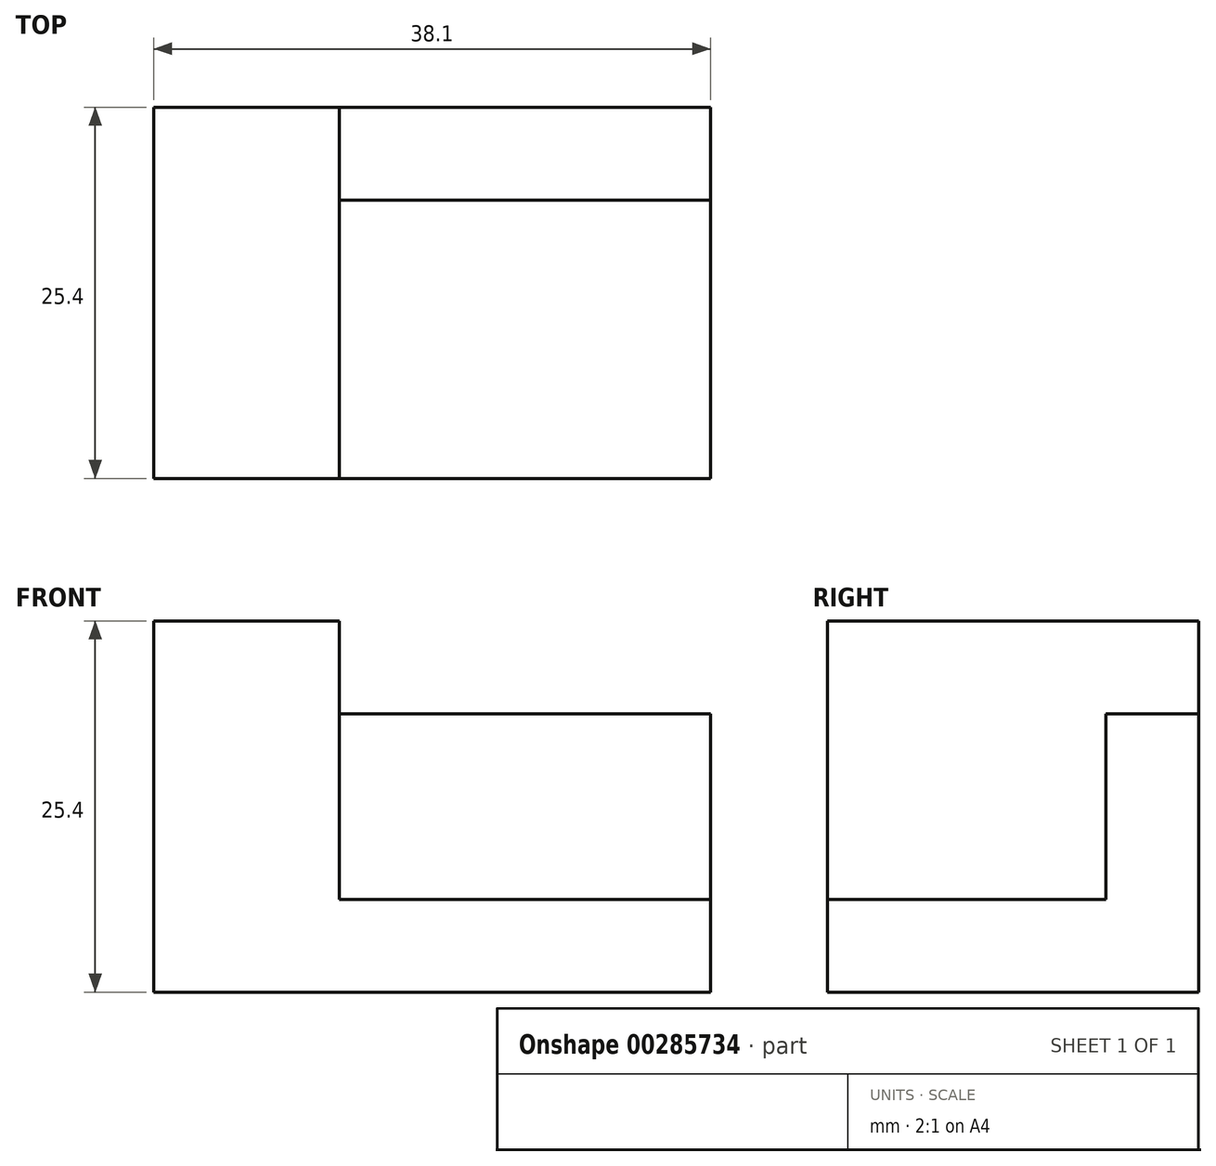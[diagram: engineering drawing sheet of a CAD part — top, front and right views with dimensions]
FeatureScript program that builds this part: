
annotation { "Feature Type Name" : "Feature", "Feature Type Description" : "" }
export const myFeature = defineFeature(function(context is Context, id is Id, definition is map)
    precondition{}
    {
        {
            var Q0;
            Q0=qCreatedBy(makeId("Front.planeOp"),FACE);
            var sketch = newSketch(context, id + "F0", { "sketchPlane" : qUnion([Q0])});
            skLineSegment(sketch, "E0", {"start": v(0, 0) * mm, "end": v(0, 25.4) * mm});
            skLineSegment(sketch, "E1", {"start": v(0, 25.4) * mm, "end": v(12.7, 25.4) * mm});
            skLineSegment(sketch, "E2", {"start": v(12.7, 25.4) * mm, "end": v(12.7, 6.35) * mm});
            skLineSegment(sketch, "E3", {"start": v(12.7, 6.35) * mm, "end": v(38.1, 6.35) * mm});
            skLineSegment(sketch, "E4", {"start": v(38.1, 6.35) * mm, "end": v(38.1, 0) * mm});
            skLineSegment(sketch, "E5", {"start": v(38.1, 0) * mm, "end": v(0, 0) * mm});
            skSolve(sketch);
        }
        {
            var Q0;
            Q0 = qSketchRegion(id + "F0", true);
            extrude(context, id + "F1", {"entities" : qUnion([Q0]), "depth" : 25.4 * mm});
        }
        {
            var Q0;
            Q0=qCreatedBy(makeId("Front.planeOp"),FACE);
            var sketch = newSketch(context, id + "F2", { "sketchPlane" : qUnion([Q0])});
            skLineSegment(sketch, "E6", {"start": v(12.7, 19.05) * mm, "end": v(38.1, 19.05) * mm});
            skLineSegment(sketch, "E7", {"start": v(38.1, 19.05) * mm, "end": v(38.1, 6.35) * mm});
            skLineSegment(sketch, "E8", {"start": v(38.1, 6.35) * mm, "end": v(12.7, 6.35) * mm});
            skLineSegment(sketch, "E9", {"start": v(12.7, 6.35) * mm, "end": v(12.7, 19.05) * mm});
            skSolve(sketch);
        }
        {
            var Q0;
            Q0 = qSketchRegion(id + "F2", true);
            extrude(context, id + "F3", {"entities" : qUnion([Q0]), "operationType" : NewBodyOperationType.ADD, "depth" : 6.35 * mm});
        }
    });
